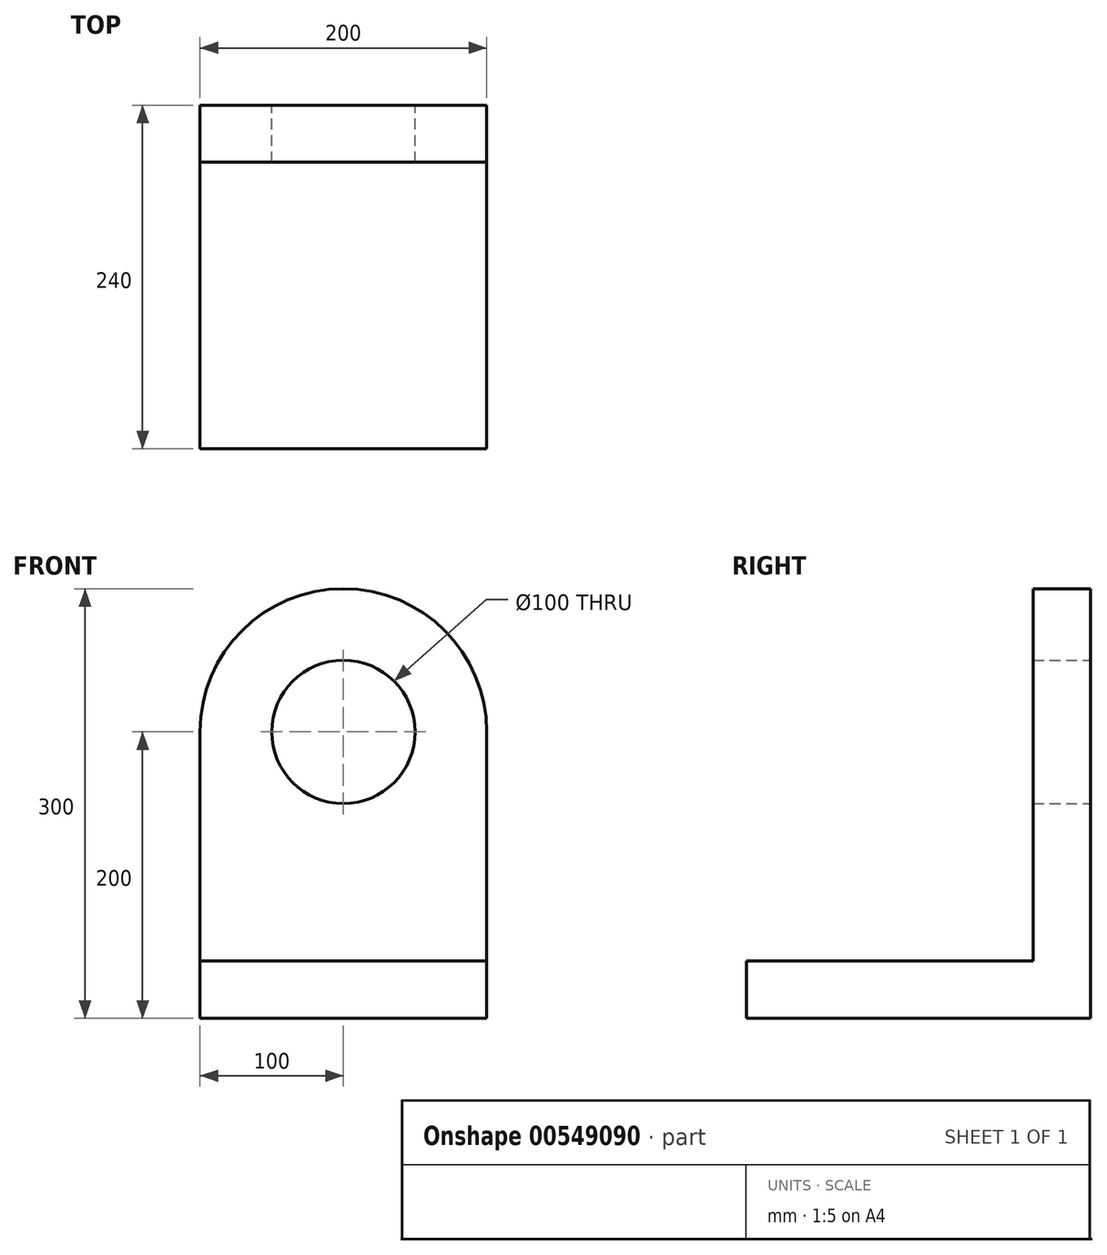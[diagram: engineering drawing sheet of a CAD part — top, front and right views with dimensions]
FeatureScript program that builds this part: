
annotation { "Feature Type Name" : "Feature", "Feature Type Description" : "" }
export const myFeature = defineFeature(function(context is Context, id is Id, definition is map)
    precondition{}
    {
        {
            var Q0;
            Q0=qCreatedBy(makeId("Front.planeOp"),FACE);
            var sketch = newSketch(context, id + "F0", { "sketchPlane" : qUnion([Q0])});
            skLineSegment(sketch, "E0.top", {"start": v(-100, 0) * mm, "end": v(100, 0) * mm});
            skLineSegment(sketch, "E0.left", {"start": v(-100, 200) * mm, "end": v(-100, 0) * mm});
            skLineSegment(sketch, "E0.right", {"start": v(100, 200) * mm, "end": v(100, 0) * mm});
            skArc(sketch, "E1", {"start": v(100, 200) * mm, "mid": v(0, 300) * mm, "end": v(-100, 200) * mm});
            skCircle(sketch, "E2", {"center": v(0, 200) * mm, "radius": 50 * mm});
            skLineSegment(sketch, "E3", {"start": v(-100, 40) * mm, "end": v(100, 40) * mm});
            skSolve(sketch);
        }
        {
            var Q0;
            Q0 = qSketchRegion(id + "F0", true);
            extrude(context, id + "F1", {"entities" : qUnion([Q0]), "endBound" : BoundingType.SYMMETRIC, "depth" : 40 * mm, "offsetDistance" : 25 * mm});
        }
        {
            var Q0;
            Q0=makeQuery(id+"F1.opExtrude","CAP_FACE",FACE,{"disambiguationData":[OSD([sQuery(id+"F0.wireOp",EDGE,"E0.top"),sQuery(id+"F0.wireOp",EDGE,"E0.left"),sQuery(id+"F0.wireOp",EDGE,"E0.right"),sQuery(id+"F0.wireOp",EDGE,"E1"),sQuery(id+"F0.wireOp",EDGE,"E2")])],"isStart":false});
            var sketch = newSketch(context, id + "F2", { "sketchPlane" : qUnion([Q0])});
            skLineSegment(sketch, "E4", {"start": v(-100, 40) * mm, "end": v(100, 40) * mm});
            skSolve(sketch);
        }
        {
            var Q0;
            {var subQ0=sQuery(id+"F2.wireOp",EDGE,"E4");Q0=makeQuery(id+"F2.imprint","IMPRINT",FACE,{"disambiguationData":[TD([[makeQuery(id+"F2.imprint","IMPRINT",EDGE,{"derivedFrom":subQ0}),-1.0]])]});}
            extrude(context, id + "F3", {"entities" : qUnion([Q0]), "operationType" : NewBodyOperationType.ADD, "depth" : 200 * mm, "offsetDistance" : 25 * mm});
        }
    });
